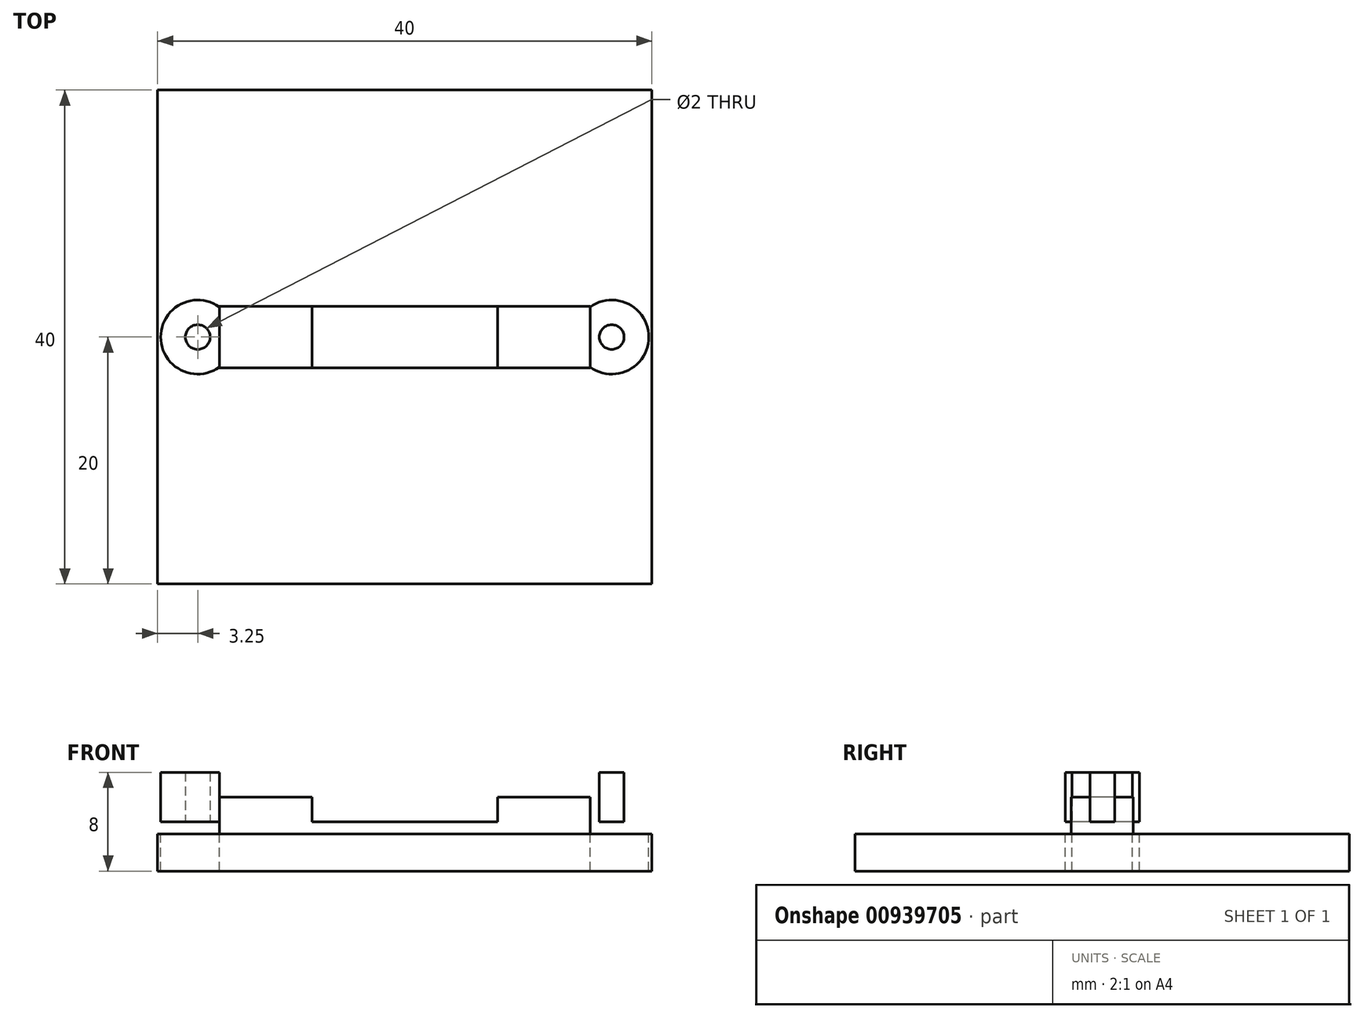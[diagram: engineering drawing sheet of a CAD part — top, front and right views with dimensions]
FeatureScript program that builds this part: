
annotation { "Feature Type Name" : "Feature", "Feature Type Description" : "" }
export const myFeature = defineFeature(function(context is Context, id is Id, definition is map)
    precondition{}
    {
        {
            var Q0;
            Q0=qCreatedBy(makeId("Top.planeOp"),FACE);
            var sketch = newSketch(context, id + "F0", { "sketchPlane" : qUnion([Q0])});
            skLineSegment(sketch, "E0.bottom", {"start": v(20, -20) * mm, "end": v(-20, -20) * mm});
            skLineSegment(sketch, "E0.top", {"start": v(20, 20) * mm, "end": v(-20, 20) * mm});
            skLineSegment(sketch, "E0.left", {"start": v(20, -20) * mm, "end": v(20, 20) * mm});
            skLineSegment(sketch, "E0.right", {"start": v(-20, -20) * mm, "end": v(-20, 20) * mm});
            skPoint(sketch, "E0.middle", {"position": v(0, 0) * mm});
            skSolve(sketch);
        }
        {
            var Q0;
            Q0 = qSketchRegion(id + "F0", true);
            extrude(context, id + "F1", {"entities" : qUnion([Q0]), "depth" : 3 * mm, "offsetDistance" : 25 * mm});
        }
        {
            var Q0;
            Q0=makeQuery(id+"F1.opExtrude","CAP_FACE",FACE,{"disambiguationData":[OSD([sQuery(id+"F0.wireOp",EDGE,"E0.bottom"),sQuery(id+"F0.wireOp",EDGE,"E0.top"),sQuery(id+"F0.wireOp",EDGE,"E0.left"),sQuery(id+"F0.wireOp",EDGE,"E0.right")])],"isStart":false});
            var sketch = newSketch(context, id + "F2", { "sketchPlane" : qUnion([Q0])});
            skLineSegment(sketch, "E1.bottom", {"start": v(-15, 2.5) * mm, "end": v(15, 2.5) * mm});
            skLineSegment(sketch, "E1.top", {"start": v(-15, -2.5) * mm, "end": v(15, -2.5) * mm});
            skLineSegment(sketch, "E1.left", {"start": v(-15, 2.5) * mm, "end": v(-15, -2.5) * mm});
            skLineSegment(sketch, "E1.right", {"start": v(15, 2.5) * mm, "end": v(15, -2.5) * mm});
            skPoint(sketch, "E1.middle", {"position": v(0, 0) * mm});
            skLineSegment(sketch, "E2", {"start": v(0, 0) * mm, "end": v(-16.75, 0) * mm});
            skPoint(sketch, "E2.endSnap0", {"position": v(-20, 0) * mm});
            skCircle(sketch, "E3", {"center": v(-16.75, 0) * mm, "radius": 3 * mm});
            skCircle(sketch, "E4", {"center": v(-16.75, 0) * mm, "radius": 1 * mm});
            skCircle(sketch, "E5.MirrorC", {"center": v(16.75, 0) * mm, "radius": 1 * mm});
            skCircle(sketch, "E6.MirrorC", {"center": v(16.75, 0) * mm, "radius": 3 * mm});
            skSolve(sketch);
        }
        {
            var Q0;
            {var subQ1=sQuery(id+"F2.wireOp",EDGE,"E1.bottom");Q0=makeQuery(id+"F2.imprint","IMPRINT",FACE,{"disambiguationData":[TD([[makeQuery(id+"F2.imprint","IMPRINT",EDGE,{"derivedFrom":subQ1}),-1.0]])]});}
            var Q1;
            {var subQ0=sQuery(id+"F2.wireOp",EDGE,"E2");var subQ1=sQuery(id+"F2.wireOp",EDGE,"E1.left");var subQ2=makeQuery(id+"F2.imprint","INTERSECT",VERTEX,{"derivedFrom":[subQ1,subQ0]});Q1=makeQuery(id+"F2.imprint","IMPRINT",FACE,{"disambiguationData":[TD([[makeQuery(id+"F2.imprint","IMPRINT",EDGE,{"disambiguationData":[TD([[subQ2,-1.0]])],"derivedFrom":subQ1}),1.0]])]});}
            var Q2;
            {var subQ0=sQuery(id+"F2.wireOp",EDGE,"E2");var subQ1=sQuery(id+"F2.wireOp",EDGE,"E1.left");var subQ2=makeQuery(id+"F2.imprint","INTERSECT",VERTEX,{"derivedFrom":[subQ1,subQ0]});Q2=makeQuery(id+"F2.imprint","IMPRINT",FACE,{"disambiguationData":[TD([[makeQuery(id+"F2.imprint","IMPRINT",EDGE,{"disambiguationData":[TD([[subQ2,1.0]])],"derivedFrom":subQ1}),1.0]])]});}
            var Q3;
            {var subQ0=sQuery(id+"F2.wireOp",EDGE,"E6.MirrorC");var subQ1=sQuery(id+"F2.wireOp",EDGE,"E1.right");var subQ2=makeQuery(id+"F2.imprint","INTERSECT",VERTEX,{"disambiguationData":[OD(0.0)],"derivedFrom":[subQ1,subQ0]});Q3=makeQuery(id+"F2.imprint","IMPRINT",FACE,{"disambiguationData":[TD([[makeQuery(id+"F2.imprint","IMPRINT",EDGE,{"disambiguationData":[TD([[subQ2,-1.0]])],"derivedFrom":subQ1}),-1.0]])]});}
            extrude(context, id + "F3", {"entities" : qUnion([Q0, Q1, Q2, Q3]), "operationType" : NewBodyOperationType.ADD, "depth" : 3 * mm, "offsetDistance" : 25 * mm});
        }
        {
            var Q0;
            Q0=makeQuery(id+"F2.imprint","IMPRINT",FACE,{"disambiguationData":[TD([[makeQuery(id+"F2.imprint","IMPRINT",EDGE,{"derivedFrom":sQuery(id+"F2.wireOp",EDGE,"E4")}),-1.0]])]});
            var Q1;
            Q1=makeQuery(id+"F2.imprint","IMPRINT",FACE,{"disambiguationData":[TD([[makeQuery(id+"F2.imprint","IMPRINT",EDGE,{"derivedFrom":sQuery(id+"F2.wireOp",EDGE,"E5.MirrorC")}),1.0]])]});
            extrude(context, id + "F4", {"entities" : qUnion([Q0, Q1]), "depth" : 5 * mm, "offsetDistance" : 25 * mm, "hasSecondDirection" : true, "secondDirectionOppositeDirection" : false, "secondDirectionDepth" : 1 * mm});
        }
        {
            var Q0;
            Q0=makeQuery(id+"F2.imprint","IMPRINT",FACE,{"disambiguationData":[TD([[makeQuery(id+"F2.imprint","IMPRINT",EDGE,{"derivedFrom":sQuery(id+"F2.wireOp",EDGE,"E4")}),-1.0]])]});
            var Q1;
            Q1=makeQuery(id+"F2.imprint","IMPRINT",FACE,{"disambiguationData":[TD([[makeQuery(id+"F2.imprint","IMPRINT",EDGE,{"derivedFrom":sQuery(id+"F2.wireOp",EDGE,"E4")}),1.0]])]});
            var Q2;
            Q2=makeQuery(id+"F2.imprint","IMPRINT",FACE,{"disambiguationData":[TD([[makeQuery(id+"F2.imprint","IMPRINT",EDGE,{"derivedFrom":sQuery(id+"F2.wireOp",EDGE,"E5.MirrorC")}),1.0]])]});
            var Q3;
            Q3=makeQuery(id+"F2.imprint","IMPRINT",FACE,{"disambiguationData":[TD([[makeQuery(id+"F2.imprint","IMPRINT",EDGE,{"derivedFrom":sQuery(id+"F2.wireOp",EDGE,"E5.MirrorC")}),-1.0]])]});
            var Q4;
            Q4=sQuery(id+"F2.wireOp",EDGE,"E3");
            var Q5;
            Q5=sQuery(id+"F2.wireOp",EDGE,"E1.left");
            var Q6;
            Q6=sQuery(id+"F2.wireOp",EDGE,"E4");
            extrude(context, id + "F5", {"entities" : qUnion([Q0, Q1, Q2, Q3]), "operationType" : NewBodyOperationType.REMOVE, "surfaceEntities" : qUnion([Q4, Q5, Q6]), "oppositeDirection" : true, "depth" : 25 * mm, "offsetDistance" : 25 * mm});
        }
        {
            var Q0;
            Q0=makeQuery(id+"F3.opExtrude","CAP_FACE",FACE,{"disambiguationData":[OSD([sQuery(id+"F2.wireOp",EDGE,"E1.bottom"),sQuery(id+"F2.wireOp",EDGE,"E1.top"),sQuery(id+"F2.wireOp",EDGE,"E1.left"),sQuery(id+"F2.wireOp",EDGE,"E1.right")])],"isStart":false});
            var sketch = newSketch(context, id + "F6", { "sketchPlane" : qUnion([Q0])});
            skLineSegment(sketch, "E7.bottom", {"start": v(-7.5, 2.5) * mm, "end": v(7.5, 2.5) * mm});
            skLineSegment(sketch, "E7.top", {"start": v(-7.5, -2.5) * mm, "end": v(7.5, -2.5) * mm});
            skLineSegment(sketch, "E7.left", {"start": v(-7.5, 2.5) * mm, "end": v(-7.5, -2.5) * mm});
            skLineSegment(sketch, "E7.right", {"start": v(7.5, 2.5) * mm, "end": v(7.5, -2.5) * mm});
            skPoint(sketch, "E7.middle", {"position": v(0, 0) * mm});
            skSolve(sketch);
        }
        {
            var Q0;
            Q0 = qSketchRegion(id + "F6", true);
            extrude(context, id + "F7", {"entities" : qUnion([Q0]), "operationType" : NewBodyOperationType.REMOVE, "oppositeDirection" : true, "depth" : 2 * mm, "offsetDistance" : 25 * mm});
        }
    });
